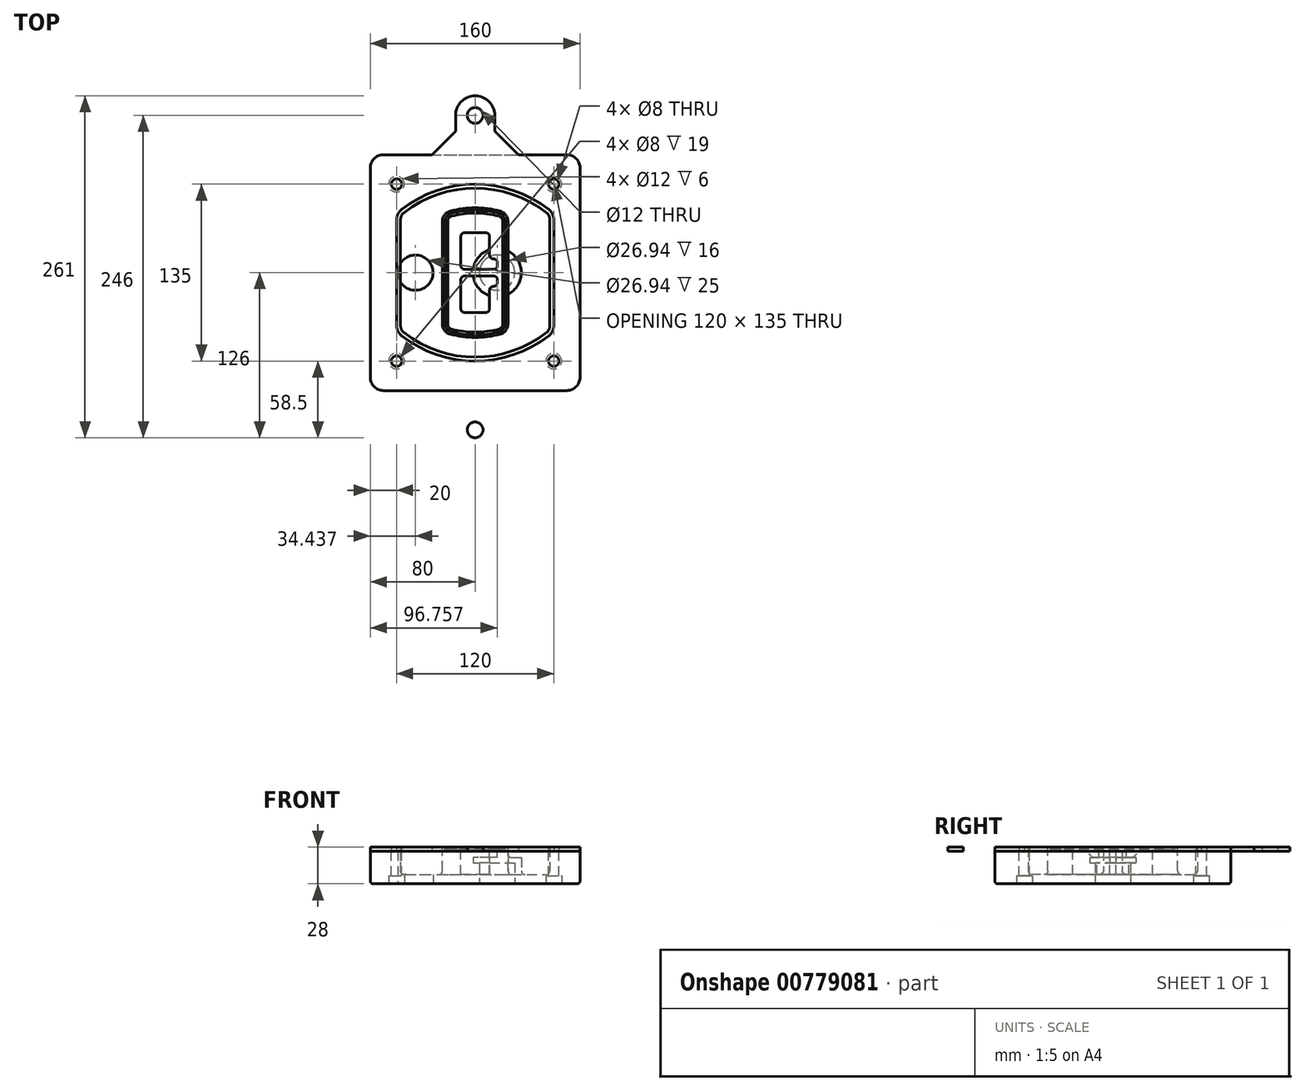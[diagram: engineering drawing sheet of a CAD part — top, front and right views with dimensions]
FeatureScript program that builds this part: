
annotation { "Feature Type Name" : "Feature", "Feature Type Description" : "" }
export const myFeature = defineFeature(function(context is Context, id is Id, definition is map)
    precondition{}
    {
        {
            var Q0;
            Q0=qCreatedBy(makeId("Top.planeOp"),FACE);
            var sketch = newSketch(context, id + "F0", { "sketchPlane" : qUnion([Q0])});
            skPoint(sketch, "E0.rect.middle", {"position": v(0, 0) * mm});
            skLineSegment(sketch, "E1.bottom", {"start": v(-70, -90) * mm, "end": v(70, -90) * mm});
            skLineSegment(sketch, "E1.top", {"start": v(-70, 90) * mm, "end": v(70, 90) * mm});
            skLineSegment(sketch, "E1.left", {"start": v(-80, -80) * mm, "end": v(-80, 80) * mm});
            skLineSegment(sketch, "E1.right", {"start": v(80, -80) * mm, "end": v(80, 80) * mm});
            skLineSegment(sketch, "E2", {"start": v(-80, 90) * mm, "end": v(80, -90) * mm, "construction": true});
            skLineSegment(sketch, "E3", {"start": v(80, 90) * mm, "end": v(-80, -90) * mm, "construction": true});
            skCircle(sketch, "E4", {"center": v(-60, 67.5) * mm, "radius": 4 * mm});
            skCircle(sketch, "E5", {"center": v(60, 67.5) * mm, "radius": 4 * mm});
            skCircle(sketch, "E6", {"center": v(60, -67.5) * mm, "radius": 4 * mm});
            skCircle(sketch, "E7", {"center": v(-60, -67.5) * mm, "radius": 4 * mm});
            skLineSegment(sketch, "E8", {"start": v(-60, 67.5) * mm, "end": v(60, 67.5) * mm, "construction": true});
            skLineSegment(sketch, "E9", {"start": v(60, 67.5) * mm, "end": v(60, -67.5) * mm, "construction": true});
            skLineSegment(sketch, "E10", {"start": v(60, -67.5) * mm, "end": v(-60, -67.5) * mm, "construction": true});
            skLineSegment(sketch, "E11", {"start": v(-60, -67.5) * mm, "end": v(-60, 67.5) * mm, "construction": true});
            skLineSegment(sketch, "E12", {"start": v(-60, 40.3) * mm, "end": v(-60, -40.3) * mm});
            skLineSegment(sketch, "E13", {"start": v(60, 40.3) * mm, "end": v(60, -40.3) * mm});
            skArc(sketch, "E14", {"start": v(56.15, 48.18) * mm, "mid": v(0, 67.5) * mm, "end": v(-56.15, 48.18) * mm});
            skArc(sketch, "E15", {"start": v(-56.15, -48.18) * mm, "mid": v(0, -67.5) * mm, "end": v(56.15, -48.18) * mm});
            skLineSegment(sketch, "E16", {"start": v(-60, 0) * mm, "end": v(60, 0) * mm, "construction": true});
            skPoint(sketch, "E17.visualSharp", {"position": v(-60, -45) * mm});
            skArc(sketch, "E17.filletArc", {"start": v(-60, -40.3) * mm, "mid": v(-58.99, -44.68) * mm, "end": v(-56.15, -48.18) * mm});
            skPoint(sketch, "E18.visualSharp", {"position": v(-60, 45) * mm});
            skArc(sketch, "E18.filletArc", {"start": v(-56.15, 48.18) * mm, "mid": v(-58.99, 44.68) * mm, "end": v(-60, 40.3) * mm});
            skPoint(sketch, "E19.visualSharp", {"position": v(60, 45) * mm});
            skArc(sketch, "E19.filletArc", {"start": v(60, 40.3) * mm, "mid": v(58.99, 44.68) * mm, "end": v(56.15, 48.18) * mm});
            skPoint(sketch, "E20.visualSharp", {"position": v(60, -45) * mm});
            skArc(sketch, "E20.filletArc", {"start": v(56.15, -48.18) * mm, "mid": v(58.99, -44.68) * mm, "end": v(60, -40.3) * mm});
            skPoint(sketch, "E21.visualSharp", {"position": v(-80, 90) * mm});
            skArc(sketch, "E21.filletArc", {"start": v(-70, 90) * mm, "mid": v(-77.07, 87.07) * mm, "end": v(-80, 80) * mm});
            skPoint(sketch, "E22.visualSharp", {"position": v(80, 90) * mm});
            skArc(sketch, "E22.filletArc", {"start": v(80, 80) * mm, "mid": v(77.07, 87.07) * mm, "end": v(70, 90) * mm});
            skPoint(sketch, "E23.visualSharp", {"position": v(80, -90) * mm});
            skArc(sketch, "E23.filletArc", {"start": v(70, -90) * mm, "mid": v(77.07, -87.07) * mm, "end": v(80, -80) * mm});
            skPoint(sketch, "E24.visualSharp", {"position": v(-80, -90) * mm});
            skArc(sketch, "E24.filletArc", {"start": v(-80, -80) * mm, "mid": v(-77.07, -87.07) * mm, "end": v(-70, -90) * mm});
            skArc(sketch, "E25.0", {"start": v(57, 40.3) * mm, "mid": v(56.3, 43.36) * mm, "end": v(54.3, 45.81) * mm});
            skLineSegment(sketch, "E25.1", {"start": v(57, 40.3) * mm, "end": v(57, -40.3) * mm});
            skArc(sketch, "E25.2", {"start": v(54.3, -45.81) * mm, "mid": v(56.3, -43.36) * mm, "end": v(57, -40.3) * mm});
            skArc(sketch, "E25.3", {"start": v(-54.3, -45.81) * mm, "mid": v(0, -64.5) * mm, "end": v(54.3, -45.81) * mm});
            skArc(sketch, "E25.4", {"start": v(-57, -40.3) * mm, "mid": v(-56.3, -43.36) * mm, "end": v(-54.3, -45.81) * mm});
            skArc(sketch, "E25.5", {"start": v(54.3, 45.81) * mm, "mid": v(0, 64.5) * mm, "end": v(-54.3, 45.81) * mm});
            skLineSegment(sketch, "E25.6", {"start": v(-57, 40.3) * mm, "end": v(-57, -40.3) * mm});
            skArc(sketch, "E25.7", {"start": v(-54.3, 45.81) * mm, "mid": v(-56.3, 43.36) * mm, "end": v(-57, 40.3) * mm});
            skArc(sketch, "E26.0", {"start": v(-58.62, 51.33) * mm, "mid": v(-62.58, 46.43) * mm, "end": v(-64, 40.3) * mm});
            skArc(sketch, "E26.1", {"start": v(58.62, 51.33) * mm, "mid": v(0, 71.5) * mm, "end": v(-58.62, 51.33) * mm});
            skArc(sketch, "E26.2", {"start": v(64, 40.3) * mm, "mid": v(62.58, 46.43) * mm, "end": v(58.62, 51.33) * mm});
            skLineSegment(sketch, "E26.3", {"start": v(64, 40.3) * mm, "end": v(64, -40.3) * mm});
            skArc(sketch, "E26.4", {"start": v(58.62, -51.33) * mm, "mid": v(62.58, -46.43) * mm, "end": v(64, -40.3) * mm});
            skLineSegment(sketch, "E26.5", {"start": v(-64, 40.3) * mm, "end": v(-64, -40.3) * mm});
            skArc(sketch, "E26.6", {"start": v(-58.62, -51.33) * mm, "mid": v(0, -71.5) * mm, "end": v(58.62, -51.33) * mm});
            skArc(sketch, "E26.7", {"start": v(-64, -40.3) * mm, "mid": v(-62.58, -46.43) * mm, "end": v(-58.62, -51.33) * mm});
            skSolve(sketch);
        }
        {
            var Q0;
            Q0=makeQuery(id+"F0.imprint","IMPRINT",FACE,{"disambiguationData":[TD([[makeQuery(id+"F0.imprint","IMPRINT",EDGE,{"derivedFrom":sQuery(id+"F0.wireOp",EDGE,"E1.bottom")}),1.0]])]});
            var Q1;
            Q1=makeQuery(id+"F0.imprint","IMPRINT",FACE,{"disambiguationData":[TD([[makeQuery(id+"F0.imprint","IMPRINT",EDGE,{"derivedFrom":sQuery(id+"F0.wireOp",EDGE,"E12")}),1.0]])]});
            var Q2;
            Q2=makeQuery(id+"F0.imprint","IMPRINT",FACE,{"disambiguationData":[TD([[makeQuery(id+"F0.imprint","IMPRINT",EDGE,{"derivedFrom":sQuery(id+"F0.wireOp",EDGE,"E25.0")}),1.0]])]});
            var Q3;
            Q3=makeQuery(id+"F0.imprint","IMPRINT",FACE,{"disambiguationData":[TD([[makeQuery(id+"F0.imprint","IMPRINT",EDGE,{"derivedFrom":sQuery(id+"F0.wireOp",EDGE,"E12")}),-1.0]])]});
            extrude(context, id + "F1", {"entities" : qUnion([Q0, Q1, Q2, Q3]), "oppositeDirection" : true, "depth" : 25 * mm});
        }
        {
            var Q0;
            Q0=makeQuery(id+"F0.imprint","IMPRINT",FACE,{"disambiguationData":[TD([[makeQuery(id+"F0.imprint","IMPRINT",EDGE,{"derivedFrom":sQuery(id+"F0.wireOp",EDGE,"E12")}),1.0]])]});
            extrude(context, id + "F2", {"entities" : qUnion([Q0]), "operationType" : NewBodyOperationType.ADD, "depth" : 3 * mm});
        }
        {
            var Q0;
            Q0=makeQuery(id+"F0.imprint","IMPRINT",FACE,{"disambiguationData":[TD([[makeQuery(id+"F0.imprint","IMPRINT",EDGE,{"derivedFrom":sQuery(id+"F0.wireOp",EDGE,"E25.0")}),1.0]])]});
            extrude(context, id + "F3", {"entities" : qUnion([Q0]), "operationType" : NewBodyOperationType.REMOVE, "oppositeDirection" : true, "depth" : 18 * mm});
        }
        {
            var Q0;
            Q0=makeQuery(id+"F2.opExtrude","CAP_FACE",FACE,{"disambiguationData":[OSD([sQuery(id+"F0.wireOp",EDGE,"E12"),sQuery(id+"F0.wireOp",EDGE,"E13"),sQuery(id+"F0.wireOp",EDGE,"E14"),sQuery(id+"F0.wireOp",EDGE,"E15"),sQuery(id+"F0.wireOp",EDGE,"E17.filletArc"),sQuery(id+"F0.wireOp",EDGE,"E18.filletArc"),sQuery(id+"F0.wireOp",EDGE,"E19.filletArc"),sQuery(id+"F0.wireOp",EDGE,"E20.filletArc"),sQuery(id+"F0.wireOp",EDGE,"E25.0"),sQuery(id+"F0.wireOp",EDGE,"E25.1"),sQuery(id+"F0.wireOp",EDGE,"E25.2"),sQuery(id+"F0.wireOp",EDGE,"E25.3"),sQuery(id+"F0.wireOp",EDGE,"E25.4"),sQuery(id+"F0.wireOp",EDGE,"E25.5"),sQuery(id+"F0.wireOp",EDGE,"E25.6"),sQuery(id+"F0.wireOp",EDGE,"E25.7")])],"isStart":false});
            var sketch = newSketch(context, id + "F4", { "sketchPlane" : qUnion([Q0])});
            skArc(sketch, "E27.0", {"start": v(-19.08, -46.97) * mm, "mid": v(0, -49.5) * mm, "end": v(19.08, -46.97) * mm});
            skArc(sketch, "E28.0", {"start": v(19.08, 46.97) * mm, "mid": v(0, 49.5) * mm, "end": v(-19.08, 46.97) * mm});
            skLineSegment(sketch, "E29", {"start": v(-25, 39.25) * mm, "end": v(-25, -39.25) * mm});
            skLineSegment(sketch, "E30", {"start": v(25, 39.25) * mm, "end": v(25, -39.25) * mm});
            skLineSegment(sketch, "E31", {"start": v(-25, 45.1) * mm, "end": v(25, 45.1) * mm, "construction": true});
            skLineSegment(sketch, "E32", {"start": v(-25, -45.1) * mm, "end": v(25, -45.1) * mm, "construction": true});
            skPoint(sketch, "E33.visualSharp", {"position": v(-25, 45.1) * mm});
            skArc(sketch, "E33.filletArc", {"start": v(-19.08, 46.97) * mm, "mid": v(-23.35, 44.11) * mm, "end": v(-25, 39.25) * mm});
            skPoint(sketch, "E34.visualSharp", {"position": v(25, 45.1) * mm});
            skArc(sketch, "E34.filletArc", {"start": v(25, 39.25) * mm, "mid": v(23.35, 44.11) * mm, "end": v(19.08, 46.97) * mm});
            skPoint(sketch, "E35.visualSharp", {"position": v(25, -45.1) * mm});
            skArc(sketch, "E35.filletArc", {"start": v(19.08, -46.97) * mm, "mid": v(23.35, -44.11) * mm, "end": v(25, -39.25) * mm});
            skPoint(sketch, "E36.visualSharp", {"position": v(-25, -45.1) * mm});
            skArc(sketch, "E36.filletArc", {"start": v(-25, -39.25) * mm, "mid": v(-23.35, -44.11) * mm, "end": v(-19.08, -46.97) * mm});
            skArc(sketch, "E37.0", {"start": v(54.3, 45.81) * mm, "mid": v(0, 64.5) * mm, "end": v(-54.3, 45.81) * mm});
            skArc(sketch, "E37.1", {"start": v(-54.3, 45.81) * mm, "mid": v(-56.3, 43.36) * mm, "end": v(-57, 40.3) * mm});
            skLineSegment(sketch, "E37.2", {"start": v(-57, 40.3) * mm, "end": v(-57, -40.3) * mm});
            skArc(sketch, "E37.3", {"start": v(-57, -40.3) * mm, "mid": v(-56.3, -43.36) * mm, "end": v(-54.3, -45.81) * mm});
            skArc(sketch, "E37.4", {"start": v(-54.3, -45.81) * mm, "mid": v(0, -64.5) * mm, "end": v(54.3, -45.81) * mm});
            skArc(sketch, "E37.5", {"start": v(54.3, -45.81) * mm, "mid": v(56.3, -43.36) * mm, "end": v(57, -40.3) * mm});
            skLineSegment(sketch, "E37.6", {"start": v(57, 40.3) * mm, "end": v(57, -40.3) * mm});
            skArc(sketch, "E37.7", {"start": v(57, 40.3) * mm, "mid": v(56.3, 43.36) * mm, "end": v(54.3, 45.81) * mm});
            skLineSegment(sketch, "E38.0", {"start": v(23, 39.25) * mm, "end": v(23, -39.25) * mm});
            skArc(sketch, "E38.1", {"start": v(18.56, -45.04) * mm, "mid": v(21.76, -42.9) * mm, "end": v(23, -39.25) * mm});
            skArc(sketch, "E38.2", {"start": v(-18.56, -45.04) * mm, "mid": v(0, -47.5) * mm, "end": v(18.56, -45.04) * mm});
            skArc(sketch, "E38.3", {"start": v(-23, -39.25) * mm, "mid": v(-21.76, -42.9) * mm, "end": v(-18.56, -45.04) * mm});
            skLineSegment(sketch, "E38.4", {"start": v(-23, 39.25) * mm, "end": v(-23, -39.25) * mm});
            skArc(sketch, "E38.5", {"start": v(23, 39.25) * mm, "mid": v(21.76, 42.9) * mm, "end": v(18.56, 45.04) * mm});
            skArc(sketch, "E38.6", {"start": v(-18.56, 45.04) * mm, "mid": v(-21.76, 42.9) * mm, "end": v(-23, 39.25) * mm});
            skArc(sketch, "E38.7", {"start": v(18.56, 45.04) * mm, "mid": v(0, 47.5) * mm, "end": v(-18.56, 45.04) * mm});
            skArc(sketch, "E39.0", {"start": v(21, 39.25) * mm, "mid": v(20.18, 41.68) * mm, "end": v(18.04, 43.1) * mm});
            skLineSegment(sketch, "E39.1", {"start": v(21, 39.25) * mm, "end": v(21, -39.25) * mm});
            skArc(sketch, "E39.2", {"start": v(18.04, -43.1) * mm, "mid": v(20.18, -41.68) * mm, "end": v(21, -39.25) * mm});
            skArc(sketch, "E39.3", {"start": v(-18.04, -43.1) * mm, "mid": v(0, -45.5) * mm, "end": v(18.04, -43.1) * mm});
            skArc(sketch, "E39.4", {"start": v(-21, -39.25) * mm, "mid": v(-20.18, -41.68) * mm, "end": v(-18.04, -43.1) * mm});
            skArc(sketch, "E39.5", {"start": v(18.04, 43.1) * mm, "mid": v(0, 45.5) * mm, "end": v(-18.04, 43.1) * mm});
            skLineSegment(sketch, "E39.6", {"start": v(-21, 39.25) * mm, "end": v(-21, -39.25) * mm});
            skArc(sketch, "E39.7", {"start": v(-18.04, 43.1) * mm, "mid": v(-20.18, 41.68) * mm, "end": v(-21, 39.25) * mm});
            skLineSegment(sketch, "E40", {"start": v(-25, 0) * mm, "end": v(25, 0) * mm, "construction": true});
            skLineSegment(sketch, "E41", {"start": v(-11, 5.5) * mm, "end": v(-11, 27.5) * mm});
            skLineSegment(sketch, "E42", {"start": v(-8, 30.5) * mm, "end": v(8, 30.5) * mm});
            skLineSegment(sketch, "E43", {"start": v(11, 27.5) * mm, "end": v(11, 13.5) * mm});
            skLineSegment(sketch, "E44", {"start": v(14, 10.5) * mm, "end": v(14, 10.5) * mm});
            skLineSegment(sketch, "E45", {"start": v(17, 7.5) * mm, "end": v(17, 5.5) * mm});
            skLineSegment(sketch, "E46", {"start": v(14, 2.5) * mm, "end": v(-8, 2.5) * mm});
            skPoint(sketch, "E47.visualSharp", {"position": v(-11, 30.5) * mm});
            skArc(sketch, "E47.filletArc", {"start": v(-8, 30.5) * mm, "mid": v(-10.12, 29.62) * mm, "end": v(-11, 27.5) * mm});
            skPoint(sketch, "E48.visualSharp", {"position": v(11, 30.5) * mm});
            skArc(sketch, "E48.filletArc", {"start": v(11, 27.5) * mm, "mid": v(10.12, 29.62) * mm, "end": v(8, 30.5) * mm});
            skPoint(sketch, "E49.visualSharp", {"position": v(11, 10.5) * mm});
            skArc(sketch, "E49.filletArc", {"start": v(11, 13.5) * mm, "mid": v(11.88, 11.38) * mm, "end": v(14, 10.5) * mm});
            skPoint(sketch, "E50.visualSharp", {"position": v(17, 10.5) * mm});
            skArc(sketch, "E50.filletArc", {"start": v(17, 7.5) * mm, "mid": v(16.12, 9.62) * mm, "end": v(14, 10.5) * mm});
            skPoint(sketch, "E51.visualSharp", {"position": v(17, 2.5) * mm});
            skArc(sketch, "E51.filletArc", {"start": v(14, 2.5) * mm, "mid": v(16.12, 3.38) * mm, "end": v(17, 5.5) * mm});
            skPoint(sketch, "E52.visualSharp", {"position": v(-11, 2.5) * mm});
            skArc(sketch, "E52.filletArc", {"start": v(-11, 5.5) * mm, "mid": v(-10.12, 3.38) * mm, "end": v(-8, 2.5) * mm});
            skLineSegment(sketch, "E53.0.MirrorCS", {"start": v(14, -2.5) * mm, "end": v(-8, -2.5) * mm});
            skArc(sketch, "E54.0.MirrorCS", {"start": v(-11, -5.5) * mm, "mid": v(-10.12, -3.38) * mm, "end": v(-8, -2.5) * mm});
            skLineSegment(sketch, "E55.0.MirrorCS", {"start": v(-11, -5.5) * mm, "end": v(-11, -27.5) * mm});
            skArc(sketch, "E56.0.MirrorCS", {"start": v(-8, -30.5) * mm, "mid": v(-10.12, -29.62) * mm, "end": v(-11, -27.5) * mm});
            skLineSegment(sketch, "E57.0.MirrorCS", {"start": v(-8, -30.5) * mm, "end": v(8, -30.5) * mm});
            skArc(sketch, "E58.0.MirrorCS", {"start": v(11, -27.5) * mm, "mid": v(10.12, -29.62) * mm, "end": v(8, -30.5) * mm});
            skLineSegment(sketch, "E59.0.MirrorCS", {"start": v(11, -27.5) * mm, "end": v(11, -13.5) * mm});
            skArc(sketch, "E60.0.MirrorCS", {"start": v(11, -13.5) * mm, "mid": v(11.88, -11.38) * mm, "end": v(14, -10.5) * mm});
            skArc(sketch, "E61.0.MirrorCS", {"start": v(17, -7.5) * mm, "mid": v(16.12, -9.62) * mm, "end": v(14, -10.5) * mm});
            skLineSegment(sketch, "E62.0.MirrorCS", {"start": v(17, -7.5) * mm, "end": v(17, -5.5) * mm});
            skArc(sketch, "E63.0.MirrorCS", {"start": v(14, -2.5) * mm, "mid": v(16.12, -3.38) * mm, "end": v(17, -5.5) * mm});
            skSolve(sketch);
        }
        {
            var Q0;
            Q0=makeQuery(id+"F4.imprint","IMPRINT",FACE,{"disambiguationData":[TD([[makeQuery(id+"F4.imprint","IMPRINT",EDGE,{"derivedFrom":sQuery(id+"F4.wireOp",EDGE,"E27.0")}),1.0]])]});
            var Q1;
            Q1=makeQuery(id+"F4.imprint","IMPRINT",FACE,{"disambiguationData":[TD([[makeQuery(id+"F4.imprint","IMPRINT",EDGE,{"derivedFrom":sQuery(id+"F4.wireOp",EDGE,"E38.0")}),-1.0]])]});
            var Q2;
            Q2=makeQuery(id+"F4.imprint","IMPRINT",FACE,{"disambiguationData":[TD([[makeQuery(id+"F4.imprint","IMPRINT",EDGE,{"derivedFrom":sQuery(id+"F4.wireOp",EDGE,"E39.0")}),1.0]])]});
            extrude(context, id + "F5", {"entities" : qUnion([Q0, Q1, Q2]), "operationType" : NewBodyOperationType.ADD, "endBound" : BoundingType.UP_TO_NEXT, "oppositeDirection" : true, "depth" : 25 * mm});
        }
        {
            var Q0;
            Q0=makeQuery(id+"F4.imprint","IMPRINT",FACE,{"disambiguationData":[TD([[makeQuery(id+"F4.imprint","IMPRINT",EDGE,{"derivedFrom":sQuery(id+"F4.wireOp",EDGE,"E38.0")}),-1.0]])]});
            extrude(context, id + "F6", {"entities" : qUnion([Q0]), "operationType" : NewBodyOperationType.REMOVE, "oppositeDirection" : true, "depth" : 2 * mm});
        }
        {
            var Q0;
            Q0=makeQuery(id+"F1.opExtrude","CAP_FACE",FACE,{"disambiguationData":[OSD([sQuery(id+"F0.wireOp",EDGE,"E1.bottom"),sQuery(id+"F0.wireOp",EDGE,"E1.top"),sQuery(id+"F0.wireOp",EDGE,"E1.left"),sQuery(id+"F0.wireOp",EDGE,"E1.right"),sQuery(id+"F0.wireOp",EDGE,"E4"),sQuery(id+"F0.wireOp",EDGE,"E5"),sQuery(id+"F0.wireOp",EDGE,"E6"),sQuery(id+"F0.wireOp",EDGE,"E7"),sQuery(id+"F0.wireOp",EDGE,"E21.filletArc"),sQuery(id+"F0.wireOp",EDGE,"E22.filletArc"),sQuery(id+"F0.wireOp",EDGE,"E23.filletArc"),sQuery(id+"F0.wireOp",EDGE,"E24.filletArc")])],"isStart":false});
            var sketch = newSketch(context, id + "F7", { "sketchPlane" : qUnion([Q0])});
            skCircle(sketch, "E64", {"center": v(16.76, 0) * mm, "radius": 13.47 * mm});
            skCircle(sketch, "E65", {"center": v(-45.56, 0) * mm, "radius": 13.47 * mm});
            skLineSegment(sketch, "E66", {"start": v(80, 0) * mm, "end": v(-80, 0) * mm});
            skCircle(sketch, "E67", {"center": v(16.76, 0) * mm, "radius": 18.47 * mm});
            skCircle(sketch, "E68", {"center": v(60, -67.5) * mm, "radius": 6 * mm});
            skCircle(sketch, "E69", {"center": v(-60, -67.5) * mm, "radius": 6 * mm});
            skCircle(sketch, "E70", {"center": v(-60, 67.5) * mm, "radius": 6 * mm});
            skCircle(sketch, "E71", {"center": v(60, 67.5) * mm, "radius": 6 * mm});
            skSolve(sketch);
        }
        {
            var Q0;
            {var subQ1=sQuery(id+"F7.wireOp",EDGE,"E66");var subQ4=sQuery(id+"F7.wireOp",EDGE,"E64");var subQ6=makeQuery(id+"F7.imprint","INTERSECT",VERTEX,{"disambiguationData":[OD(0.0)],"derivedFrom":[subQ4,subQ1]});Q0=makeQuery(id+"F7.imprint","IMPRINT",FACE,{"disambiguationData":[TD([[makeQuery(id+"F7.imprint","IMPRINT",EDGE,{"disambiguationData":[TD([[subQ6,-1.0]])],"derivedFrom":subQ4}),-1.0]])]});}
            var Q1;
            {var subQ0=sQuery(id+"F7.wireOp",EDGE,"E66");var subQ1=sQuery(id+"F7.wireOp",EDGE,"E64");var subQ3=makeQuery(id+"F7.imprint","INTERSECT",VERTEX,{"disambiguationData":[OD(0.0)],"derivedFrom":[subQ1,subQ0]});Q1=makeQuery(id+"F7.imprint","IMPRINT",FACE,{"disambiguationData":[TD([[makeQuery(id+"F7.imprint","IMPRINT",EDGE,{"disambiguationData":[TD([[subQ3,-1.0]])],"derivedFrom":subQ1}),1.0]])]});}
            var Q2;
            {var subQ0=sQuery(id+"F7.wireOp",EDGE,"E66");var subQ1=sQuery(id+"F7.wireOp",EDGE,"E64");var subQ3=makeQuery(id+"F7.imprint","INTERSECT",VERTEX,{"disambiguationData":[OD(0.0)],"derivedFrom":[subQ1,subQ0]});Q2=makeQuery(id+"F7.imprint","IMPRINT",FACE,{"disambiguationData":[TD([[makeQuery(id+"F7.imprint","IMPRINT",EDGE,{"disambiguationData":[TD([[subQ3,1.0]])],"derivedFrom":subQ1}),1.0]])]});}
            var Q3;
            {var subQ1=sQuery(id+"F7.wireOp",EDGE,"E66");var subQ4=sQuery(id+"F7.wireOp",EDGE,"E64");var subQ6=makeQuery(id+"F7.imprint","INTERSECT",VERTEX,{"disambiguationData":[OD(0.0)],"derivedFrom":[subQ4,subQ1]});Q3=makeQuery(id+"F7.imprint","IMPRINT",FACE,{"disambiguationData":[TD([[makeQuery(id+"F7.imprint","IMPRINT",EDGE,{"disambiguationData":[TD([[subQ6,1.0]])],"derivedFrom":subQ4}),-1.0]])]});}
            extrude(context, id + "F8", {"entities" : qUnion([Q0, Q1, Q2, Q3]), "operationType" : NewBodyOperationType.ADD, "oppositeDirection" : true, "depth" : 20 * mm});
        }
        {
            var Q0;
            {var subQ0=sQuery(id+"F7.wireOp",EDGE,"E66");var subQ1=sQuery(id+"F7.wireOp",EDGE,"E64");var subQ3=makeQuery(id+"F7.imprint","INTERSECT",VERTEX,{"disambiguationData":[OD(0.0)],"derivedFrom":[subQ1,subQ0]});Q0=makeQuery(id+"F7.imprint","IMPRINT",FACE,{"disambiguationData":[TD([[makeQuery(id+"F7.imprint","IMPRINT",EDGE,{"disambiguationData":[TD([[subQ3,-1.0]])],"derivedFrom":subQ1}),1.0]])]});}
            var Q1;
            {var subQ0=sQuery(id+"F7.wireOp",EDGE,"E66");var subQ1=sQuery(id+"F7.wireOp",EDGE,"E64");var subQ3=makeQuery(id+"F7.imprint","INTERSECT",VERTEX,{"disambiguationData":[OD(0.0)],"derivedFrom":[subQ1,subQ0]});Q1=makeQuery(id+"F7.imprint","IMPRINT",FACE,{"disambiguationData":[TD([[makeQuery(id+"F7.imprint","IMPRINT",EDGE,{"disambiguationData":[TD([[subQ3,1.0]])],"derivedFrom":subQ1}),1.0]])]});}
            extrude(context, id + "F9", {"entities" : qUnion([Q0, Q1]), "operationType" : NewBodyOperationType.REMOVE, "oppositeDirection" : true, "depth" : 16 * mm});
        }
        {
            var Q0;
            {var subQ0=sQuery(id+"F7.wireOp",EDGE,"E66");var subQ1=sQuery(id+"F7.wireOp",EDGE,"E65");var subQ3=makeQuery(id+"F7.imprint","INTERSECT",VERTEX,{"disambiguationData":[OD(0.0)],"derivedFrom":[subQ1,subQ0]});Q0=makeQuery(id+"F7.imprint","IMPRINT",FACE,{"disambiguationData":[TD([[makeQuery(id+"F7.imprint","IMPRINT",EDGE,{"disambiguationData":[TD([[subQ3,-1.0]])],"derivedFrom":subQ1}),1.0]])]});}
            var Q1;
            {var subQ0=sQuery(id+"F7.wireOp",EDGE,"E66");var subQ1=sQuery(id+"F7.wireOp",EDGE,"E65");var subQ3=makeQuery(id+"F7.imprint","INTERSECT",VERTEX,{"disambiguationData":[OD(0.0)],"derivedFrom":[subQ1,subQ0]});Q1=makeQuery(id+"F7.imprint","IMPRINT",FACE,{"disambiguationData":[TD([[makeQuery(id+"F7.imprint","IMPRINT",EDGE,{"disambiguationData":[TD([[subQ3,1.0]])],"derivedFrom":subQ1}),1.0]])]});}
            extrude(context, id + "F10", {"entities" : qUnion([Q0, Q1]), "operationType" : NewBodyOperationType.REMOVE, "oppositeDirection" : true, "depth" : 25 * mm});
        }
        {
            var Q0;
            Q0=makeQuery(id+"F7.imprint","IMPRINT",FACE,{"disambiguationData":[TD([[makeQuery(id+"F7.imprint","IMPRINT",EDGE,{"derivedFrom":sQuery(id+"F7.wireOp",EDGE,"E68")}),1.0]])]});
            var Q1;
            Q1=makeQuery(id+"F7.imprint","IMPRINT",FACE,{"disambiguationData":[TD([[makeQuery(id+"F7.imprint","IMPRINT",EDGE,{"derivedFrom":makeQuery(id+"F1.opExtrude","CAP_EDGE",EDGE,{"disambiguationData":[OSD([sQuery(id+"F0.wireOp",EDGE,"E5")])],"isStart":false})}),-1.0]])]});
            var Q2;
            Q2=makeQuery(id+"F7.imprint","IMPRINT",FACE,{"disambiguationData":[TD([[makeQuery(id+"F7.imprint","IMPRINT",EDGE,{"derivedFrom":sQuery(id+"F7.wireOp",EDGE,"E69")}),1.0]])]});
            var Q3;
            Q3=makeQuery(id+"F7.imprint","IMPRINT",FACE,{"disambiguationData":[TD([[makeQuery(id+"F7.imprint","IMPRINT",EDGE,{"derivedFrom":makeQuery(id+"F1.opExtrude","CAP_EDGE",EDGE,{"disambiguationData":[OSD([sQuery(id+"F0.wireOp",EDGE,"E4")])],"isStart":false})}),-1.0]])]});
            var Q4;
            Q4=makeQuery(id+"F7.imprint","IMPRINT",FACE,{"disambiguationData":[TD([[makeQuery(id+"F7.imprint","IMPRINT",EDGE,{"derivedFrom":sQuery(id+"F7.wireOp",EDGE,"E70")}),1.0]])]});
            var Q5;
            Q5=makeQuery(id+"F7.imprint","IMPRINT",FACE,{"disambiguationData":[TD([[makeQuery(id+"F7.imprint","IMPRINT",EDGE,{"derivedFrom":makeQuery(id+"F1.opExtrude","CAP_EDGE",EDGE,{"disambiguationData":[OSD([sQuery(id+"F0.wireOp",EDGE,"E7")])],"isStart":false})}),-1.0]])]});
            var Q6;
            Q6=makeQuery(id+"F7.imprint","IMPRINT",FACE,{"disambiguationData":[TD([[makeQuery(id+"F7.imprint","IMPRINT",EDGE,{"derivedFrom":sQuery(id+"F7.wireOp",EDGE,"E71")}),1.0]])]});
            var Q7;
            Q7=makeQuery(id+"F7.imprint","IMPRINT",FACE,{"disambiguationData":[TD([[makeQuery(id+"F7.imprint","IMPRINT",EDGE,{"derivedFrom":makeQuery(id+"F1.opExtrude","CAP_EDGE",EDGE,{"disambiguationData":[OSD([sQuery(id+"F0.wireOp",EDGE,"E6")])],"isStart":false})}),-1.0]])]});
            extrude(context, id + "F11", {"entities" : qUnion([Q0, Q1, Q2, Q3, Q4, Q5, Q6, Q7]), "operationType" : NewBodyOperationType.REMOVE, "oppositeDirection" : true, "depth" : 6 * mm});
        }
        {
            var Q0;
            Q0=makeQuery(id+"F9.boolean.opBoolean","COPY",FACE,{"derivedFrom":makeQuery(id+"F9.opExtrude","CAP_FACE",FACE,{"disambiguationData":[OSD([sQuery(id+"F7.wireOp",EDGE,"E64")])],"isStart":false})});
            var sketch = newSketch(context, id + "F12", { "sketchPlane" : qUnion([Q0])});
            skArc(sketch, "E72.0", {"start": v(11, 17.55) * mm, "mid": v(2.57, 11.82) * mm, "end": v(-1.54, 2.5) * mm});
            skArc(sketch, "E72.1", {"start": v(-1.54, -2.5) * mm, "mid": v(2.57, -11.82) * mm, "end": v(11, -17.55) * mm});
            skLineSegment(sketch, "E73", {"start": v(-1.54, -2.5) * mm, "end": v(14, -2.5) * mm});
            skLineSegment(sketch, "E74.0", {"start": v(14, 2.5) * mm, "end": v(-1.54, 2.5) * mm});
            skArc(sketch, "E74.1", {"start": v(14, 2.5) * mm, "mid": v(16.12, 3.38) * mm, "end": v(17, 5.5) * mm});
            skLineSegment(sketch, "E74.2", {"start": v(17, 7.5) * mm, "end": v(17, 5.5) * mm});
            skArc(sketch, "E74.3", {"start": v(17, 7.5) * mm, "mid": v(16.12, 9.62) * mm, "end": v(14, 10.5) * mm});
            skArc(sketch, "E74.4", {"start": v(11, 13.5) * mm, "mid": v(11.88, 11.38) * mm, "end": v(14, 10.5) * mm});
            skLineSegment(sketch, "E74.5", {"start": v(11, 17.55) * mm, "end": v(11, 13.5) * mm});
            skLineSegment(sketch, "E74.7", {"start": v(14, -2.5) * mm, "end": v(-1.54, -2.5) * mm});
            skArc(sketch, "E74.8", {"start": v(14, -2.5) * mm, "mid": v(16.12, -3.38) * mm, "end": v(17, -5.5) * mm});
            skLineSegment(sketch, "E74.9", {"start": v(17, -7.5) * mm, "end": v(17, -5.5) * mm});
            skArc(sketch, "E74.10", {"start": v(17, -7.5) * mm, "mid": v(16.12, -9.62) * mm, "end": v(14, -10.5) * mm});
            skArc(sketch, "E74.11", {"start": v(11, -13.5) * mm, "mid": v(11.88, -11.38) * mm, "end": v(14, -10.5) * mm});
            skLineSegment(sketch, "E74.12", {"start": v(11, -17.55) * mm, "end": v(11, -13.5) * mm});
            skPoint(sketch, "E75.orphan", {"position": v(11, -27.5) * mm});
            skPoint(sketch, "E76.orphan", {"position": v(-8, -2.5) * mm});
            skPoint(sketch, "E77.orphan", {"position": v(-8, 2.5) * mm});
            skPoint(sketch, "E78.orphan", {"position": v(11, 27.5) * mm});
            skSolve(sketch);
        }
        {
            var Q0;
            {var subQ7=sQuery(id+"F12.wireOp",EDGE,"E72.0");var subQ14=sQuery(id+"F12.wireOp",EDGE,"E72.1");var subQ16=sQuery(id+"F12.wireOp",EDGE,"E74.1");var subQ18=sQuery(id+"F12.wireOp",EDGE,"E74.8");Q0=qUnion([makeQuery(id+"F12.imprint","IMPRINT",FACE,{"disambiguationData":[TD([[makeQuery(id+"F12.imprint","IMPRINT",EDGE,{"derivedFrom":subQ7}),1.0]])]}),makeQuery(id+"F12.imprint","IMPRINT",FACE,{"disambiguationData":[TD([[makeQuery(id+"F12.imprint","IMPRINT",EDGE,{"derivedFrom":subQ14}),1.0]])]}),makeQuery(id+"F12.imprint","IMPRINT",FACE,{"disambiguationData":[TD([[makeQuery(id+"F12.imprint","IMPRINT",EDGE,{"derivedFrom":subQ16}),1.0]])]}),makeQuery(id+"F12.imprint","IMPRINT",FACE,{"disambiguationData":[TD([[makeQuery(id+"F12.imprint","IMPRINT",EDGE,{"derivedFrom":subQ18}),-1.0]])]})]);}
            var Q1;
            Q1=makeQuery(id+"F5.boolean.opBoolean","SPLIT",FACE,{"disambiguationData":[TD([makeQuery(id+"F5.opExtrude","SWEPT_FACE",FACE,{"disambiguationData":[OSD([sQuery(id+"F4.wireOp",EDGE,"E41")])]})])],"derivedFrom":makeQuery(id+"F3.boolean.opBoolean","COPY",FACE,{"derivedFrom":makeQuery(id+"F3.opExtrude","CAP_FACE",FACE,{"disambiguationData":[OSD([sQuery(id+"F0.wireOp",EDGE,"E25.0"),sQuery(id+"F0.wireOp",EDGE,"E25.1"),sQuery(id+"F0.wireOp",EDGE,"E25.2"),sQuery(id+"F0.wireOp",EDGE,"E25.3"),sQuery(id+"F0.wireOp",EDGE,"E25.4"),sQuery(id+"F0.wireOp",EDGE,"E25.5"),sQuery(id+"F0.wireOp",EDGE,"E25.6"),sQuery(id+"F0.wireOp",EDGE,"E25.7")])],"isStart":false})})});
            extrude(context, id + "F13", {"entities" : qUnion([Q0]), "operationType" : NewBodyOperationType.REMOVE, "endBound" : BoundingType.UP_TO_SURFACE, "endBoundEntityFace" : qUnion([Q1]), "depth" : 25 * mm});
        }
        {
            var Q0;
            Q0=makeQuery(id+"F3.boolean.opBoolean","COPY",EDGE,{"derivedFrom":makeQuery(id+"F3.opExtrude","CAP_EDGE",EDGE,{"disambiguationData":[OSD([sQuery(id+"F0.wireOp",EDGE,"E25.6")])],"isStart":false})});
            var Q1;
            Q1=makeQuery(id+"F8.boolean.opBoolean","INTERSECT",EDGE,{"derivedFrom":[makeQuery(id+"F5.opExtrude","SWEPT_FACE",FACE,{"disambiguationData":[OSD([sQuery(id+"F4.wireOp",EDGE,"E30")])]}),makeQuery(id+"F8.opExtrude","CAP_FACE",FACE,{"disambiguationData":[OSD([sQuery(id+"F7.wireOp",EDGE,"E67")])],"isStart":false})]});
            var Q2;
            Q2=makeQuery(id+"F8.boolean.opBoolean","INTERSECT",EDGE,{"disambiguationData":[OD(1.0)],"derivedFrom":[makeQuery(id+"F5.opExtrude","SWEPT_FACE",FACE,{"disambiguationData":[OSD([sQuery(id+"F4.wireOp",EDGE,"E30")])]}),makeQuery(id+"F8.opExtrude","SWEPT_FACE",FACE,{"disambiguationData":[OSD([sQuery(id+"F7.wireOp",EDGE,"E67")])]})]});
            var Q3;
            {var subQ0=sQuery(id+"F4.wireOp",EDGE,"E30");Q3=makeQuery(id+"F8.boolean.opBoolean","SPLIT",EDGE,{"disambiguationData":[TD([makeQuery(id+"F5.opExtrude","SWEPT_FACE",FACE,{"disambiguationData":[OSD([sQuery(id+"F4.wireOp",EDGE,"E35.filletArc")])]})])],"derivedFrom":makeQuery(id+"F5.opExtrude","CAP_EDGE",EDGE,{"disambiguationData":[OSD([subQ0])],"isStart":false})});}
            var Q4;
            {var subQ0=sQuery(id+"F0.wireOp",EDGE,"E25.7");var subQ1=sQuery(id+"F0.wireOp",EDGE,"E25.1");var subQ2=sQuery(id+"F0.wireOp",EDGE,"E25.6");var subQ3=sQuery(id+"F0.wireOp",EDGE,"E25.5");var subQ4=sQuery(id+"F0.wireOp",EDGE,"E25.4");var subQ5=sQuery(id+"F0.wireOp",EDGE,"E25.0");var subQ6=sQuery(id+"F0.wireOp",EDGE,"E25.2");var subQ7=sQuery(id+"F0.wireOp",EDGE,"E25.3");Q4=makeQuery(id+"F8.boolean.opBoolean","INTERSECT",EDGE,{"derivedFrom":[makeQuery(id+"F5.boolean.opBoolean","SPLIT",FACE,{"disambiguationData":[TD([makeQuery(id+"F2.opExtrude","SWEPT_FACE",FACE,{"disambiguationData":[OSD([subQ5])]})])],"derivedFrom":makeQuery(id+"F3.boolean.opBoolean","COPY",FACE,{"derivedFrom":makeQuery(id+"F3.opExtrude","CAP_FACE",FACE,{"disambiguationData":[OSD([subQ5,subQ1,subQ6,subQ7,subQ4,subQ3,subQ2,subQ0])],"isStart":false})})}),makeQuery(id+"F8.opExtrude","SWEPT_FACE",FACE,{"disambiguationData":[OSD([sQuery(id+"F7.wireOp",EDGE,"E67")])]})]});}
            var Q5;
            Q5=makeQuery(id+"F8.boolean.opBoolean","INTERSECT",EDGE,{"disambiguationData":[OD(0.0)],"derivedFrom":[makeQuery(id+"F5.opExtrude","SWEPT_FACE",FACE,{"disambiguationData":[OSD([sQuery(id+"F4.wireOp",EDGE,"E30")])]}),makeQuery(id+"F8.opExtrude","SWEPT_FACE",FACE,{"disambiguationData":[OSD([sQuery(id+"F7.wireOp",EDGE,"E67")])]})]});
            fillet(context, id + "F14", {"entities" : qUnion([Q0, Q1, Q2, Q3, Q4, Q5]), "radius" : 3 * mm, "tangentPropagation" : true, "allowEdgeOverflow" : false});
        }
        {
            var Q0;
            Q0=makeQuery(id+"F1.opExtrude","CAP_EDGE",EDGE,{"disambiguationData":[OSD([sQuery(id+"F0.wireOp",EDGE,"E1.bottom")])],"isStart":false});
            fillet(context, id + "F15", {"entities" : qUnion([Q0]), "radius" : 2 * mm, "tangentPropagation" : true, "allowEdgeOverflow" : false});
        }
        {
            var Q0;
            {var subQ0=sQuery(id+"F0.wireOp",EDGE,"E21.filletArc");var subQ1=sQuery(id+"F0.wireOp",EDGE,"E7");var subQ2=sQuery(id+"F0.wireOp",EDGE,"E6");var subQ3=sQuery(id+"F0.wireOp",EDGE,"E5");var subQ4=sQuery(id+"F0.wireOp",EDGE,"E4");var subQ5=sQuery(id+"F0.wireOp",EDGE,"E22.filletArc");var subQ6=sQuery(id+"F0.wireOp",EDGE,"E1.bottom");var subQ7=sQuery(id+"F0.wireOp",EDGE,"E1.right");var subQ8=sQuery(id+"F0.wireOp",EDGE,"E1.top");var subQ9=sQuery(id+"F0.wireOp",EDGE,"E1.left");var subQ10=sQuery(id+"F0.wireOp",EDGE,"E23.filletArc");var subQ11=sQuery(id+"F0.wireOp",EDGE,"E24.filletArc");Q0=makeQuery(id+"F2.boolean.opBoolean","SPLIT",FACE,{"disambiguationData":[TD([makeQuery(id+"F1.opExtrude","SWEPT_FACE",FACE,{"disambiguationData":[OSD([subQ6])]})])],"derivedFrom":makeQuery(id+"F1.opExtrude","CAP_FACE",FACE,{"disambiguationData":[OSD([subQ6,subQ8,subQ9,subQ7,subQ4,subQ3,subQ2,subQ1,subQ0,subQ5,subQ10,subQ11])],"isStart":true})});}
            var sketch = newSketch(context, id + "F16", { "sketchPlane" : qUnion([Q0])});
            skLineSegment(sketch, "E79", {"start": v(0, 90) * mm, "end": v(0, 120) * mm, "construction": true});
            skCircle(sketch, "E80", {"center": v(0, 120) * mm, "radius": 6 * mm});
            skArc(sketch, "E81", {"start": v(15, 120) * mm, "mid": v(0, 135) * mm, "end": v(-15, 120) * mm});
            skLineSegment(sketch, "E82", {"start": v(-15, 120) * mm, "end": v(-15, 108) * mm});
            skLineSegment(sketch, "E83", {"start": v(-15, 108) * mm, "end": v(-33, 90) * mm});
            skLineSegment(sketch, "E84", {"start": v(15, 120) * mm, "end": v(15, 108) * mm});
            skLineSegment(sketch, "E85", {"start": v(15, 108) * mm, "end": v(33, 90) * mm});
            skLineSegment(sketch, "E86", {"start": v(-80, 0) * mm, "end": v(80, 0) * mm, "construction": true});
            skCircle(sketch, "E87.MirrorC", {"center": v(0, -120) * mm, "radius": 6 * mm});
            skLineSegment(sketch, "E88.MirrorCS", {"start": v(-15, -120) * mm, "end": v(-15, -108) * mm});
            skLineSegment(sketch, "E89.MirrorCS", {"start": v(15, -120) * mm, "end": v(15, -108) * mm});
            skLineSegment(sketch, "E90.MirrorCS", {"start": v(15, -108) * mm, "end": v(33, -90) * mm});
            skArc(sketch, "E91.MirrorCS", {"start": v(15, -120) * mm, "mid": v(0, -135) * mm, "end": v(-15, -120) * mm});
            skLineSegment(sketch, "E92.MirrorCS", {"start": v(-15, -108) * mm, "end": v(-33, -90) * mm});
            skLineSegment(sketch, "E93.MirrorCS", {"start": v(0, -90) * mm, "end": v(0, -120) * mm, "construction": true});
            skSolve(sketch);
        }
        {
            var Q0;
            Q0=makeQuery(id+"F16.imprint","IMPRINT",FACE,{"disambiguationData":[TD([[makeQuery(id+"F16.imprint","IMPRINT",EDGE,{"derivedFrom":sQuery(id+"F16.wireOp",EDGE,"E80")}),-1.0]])]});
            var Q1;
            Q1=makeQuery(id+"F16.imprint","IMPRINT",FACE,{"disambiguationData":[TD([[makeQuery(id+"F16.imprint","IMPRINT",EDGE,{"derivedFrom":makeQuery(id+"F1.opExtrude","CAP_EDGE",EDGE,{"disambiguationData":[OSD([sQuery(id+"F0.wireOp",EDGE,"E1.left")])],"isStart":true})}),-1.0]])]});
            var Q2;
            Q2=makeQuery(id+"F16.imprint","IMPRINT",FACE,{"disambiguationData":[TD([[makeQuery(id+"F16.imprint","IMPRINT",EDGE,{"derivedFrom":sQuery(id+"F16.wireOp",EDGE,"E87.MirrorC")}),1.0]])]});
            var Q3;
            Q3=makeQuery(id+"F2.opExtrude","CAP_FACE",FACE,{"disambiguationData":[OSD([sQuery(id+"F0.wireOp",EDGE,"E12"),sQuery(id+"F0.wireOp",EDGE,"E13"),sQuery(id+"F0.wireOp",EDGE,"E14"),sQuery(id+"F0.wireOp",EDGE,"E15"),sQuery(id+"F0.wireOp",EDGE,"E17.filletArc"),sQuery(id+"F0.wireOp",EDGE,"E18.filletArc"),sQuery(id+"F0.wireOp",EDGE,"E19.filletArc"),sQuery(id+"F0.wireOp",EDGE,"E20.filletArc"),sQuery(id+"F0.wireOp",EDGE,"E25.0"),sQuery(id+"F0.wireOp",EDGE,"E25.1"),sQuery(id+"F0.wireOp",EDGE,"E25.2"),sQuery(id+"F0.wireOp",EDGE,"E25.3"),sQuery(id+"F0.wireOp",EDGE,"E25.4"),sQuery(id+"F0.wireOp",EDGE,"E25.5"),sQuery(id+"F0.wireOp",EDGE,"E25.6"),sQuery(id+"F0.wireOp",EDGE,"E25.7")])],"isStart":false});
            extrude(context, id + "F17", {"entities" : qUnion([Q0, Q1, Q2]), "endBound" : BoundingType.UP_TO_SURFACE, "depth" : 25 * mm, "endBoundEntityFace" : qUnion([Q3]), "offsetDistance" : 25 * mm});
        }
    });
